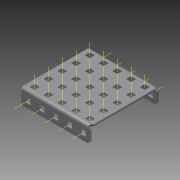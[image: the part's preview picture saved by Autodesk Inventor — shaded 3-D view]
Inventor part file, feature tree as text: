
AUTODESK INVENTOR PART (.ipt)
format: ipt  version: 2015 (Build 190159000, 159)  size: 2,339,328 bytes
history: native  units: in
note: dims shown in document units (in); Inventor stores cm internally (conversion verified against a paired STEP export)
features: other x41, pattern_linear x2, sheet_metal_op x1, extrude x1, imported_body x1, sketch x1
ambient origin geometry x8: Origin, YZ Plane, XZ Plane, XY Plane, X Axis, Y Axis, Z Axis, Center Point
bodies: Body1 (feature_tree)
feature tree (47):
  sheet_metal_op  "Fold1"
  other  "C-Channel"
  extrude  "length cut"  Depth=0.5in
  other  "top axis"
  other  "front axis"
  other  "back axis"
  pattern_linear  "top axes"  Spacing1=0.5in  [1 undecoded]
  pattern_linear  "horiz axes"  Spacing1=0.0in  [1 undecoded]
  other  "right plane"
  imported_body  "Base1"
  sketch  "Sketch1"  dims[d1=0.0in d4=0.5in d5=1.9685in d7=0.5in d10=0.5in d11=0.0in d12=0.0in d13=0.0in d14=-2.5in d15=0.0in d16=0.0in]
  other  "Work Point1"
  other  "Work Axis6"
  other  "Work Axis11"
  other  "Work Axis16"
  other  "Work Axis21"
  other  "Work Point2"
  other  "Work Point3"
  other  "Work Axis36"
  other  "Work Axis37"
  other  "Work Axis38"
  other  "Work Axis39"
  other  "Work Axis60"
  other  "Work Axis61"
  other  "Work Axis62"
  other  "Work Axis63"
  other  "Work Axis84"
  other  "Work Axis85"
  other  "Work Axis86"
  other  "Work Axis87"
  other  "Work Axis108"
  other  "Work Axis109"
  other  "Work Axis110"
  other  "Work Axis111"
  other  "Work Axis132"
  other  "Work Axis133"
  other  "Work Axis134"
  other  "Work Axis135"
  other  "Work Axis156"
  other  "Work Axis157"
  other  "Work Axis158"
  other  "Work Axis159"
  other  "Work Axis180"
  other  "Work Axis181"
  other  "Work Axis182"
  other  "Work Axis183"
  other  "left plane"
note: 2 required parameter values undecoded (feature->parameter linkage not recoverable at this tier; creation-order binding heuristic only, values carry confidence <= 0.55)
